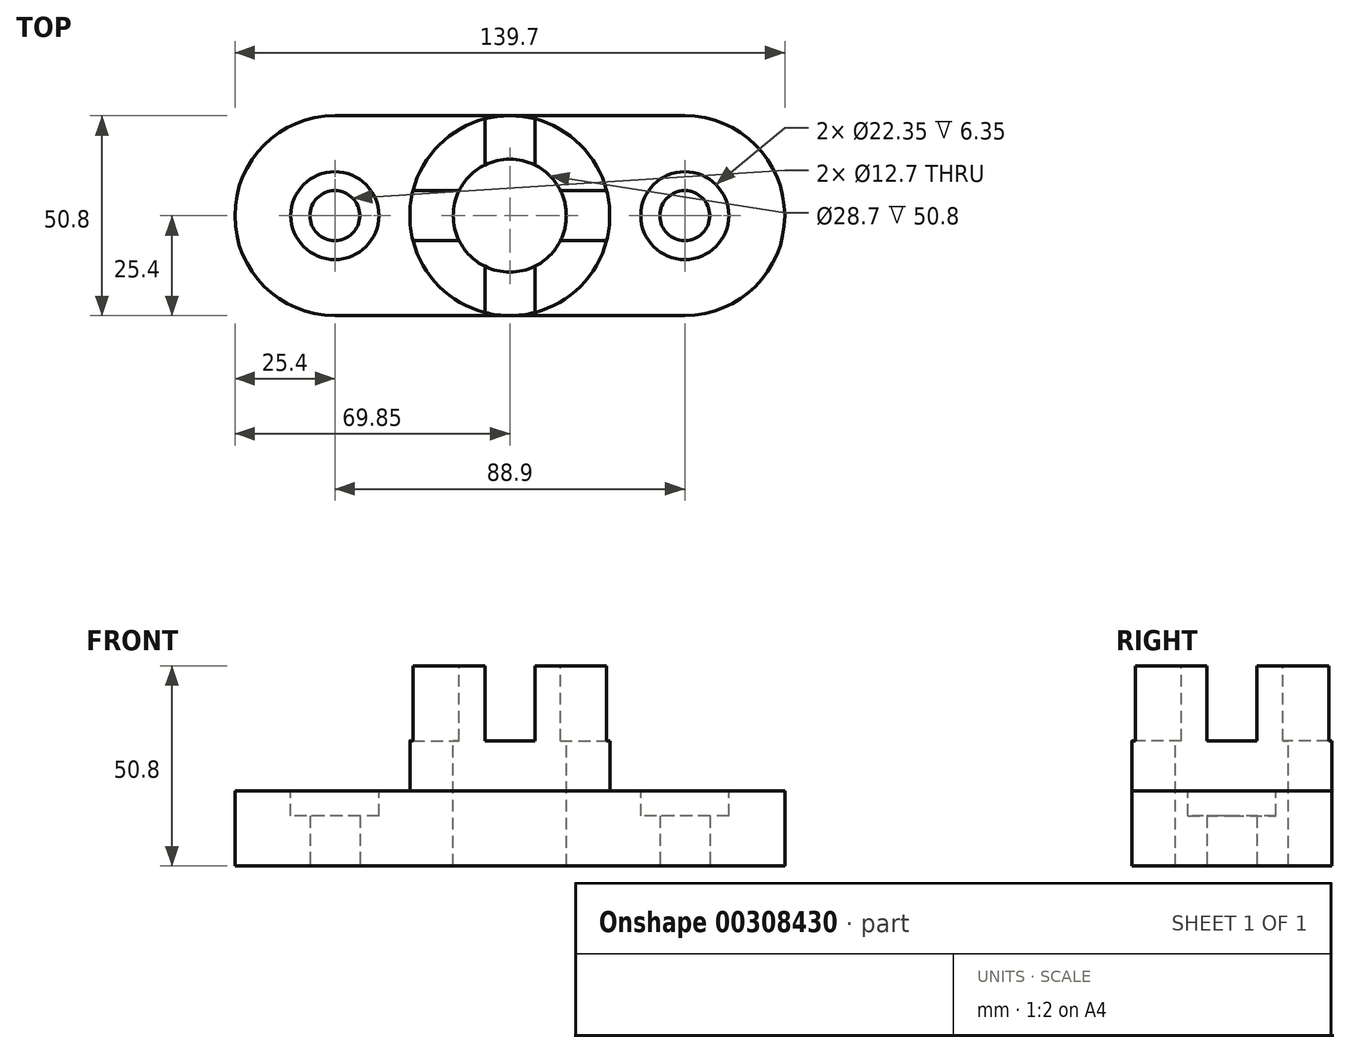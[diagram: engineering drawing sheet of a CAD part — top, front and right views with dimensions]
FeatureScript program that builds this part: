
annotation { "Feature Type Name" : "Feature", "Feature Type Description" : "" }
export const myFeature = defineFeature(function(context is Context, id is Id, definition is map)
    precondition{}
    {
        {
            var Q0;
            Q0=qCreatedBy(makeId("Front.planeOp"),FACE);
            var sketch = newSketch(context, id + "F0", { "sketchPlane" : qUnion([Q0])});
            skLineSegment(sketch, "E0", {"start": v(0, 0) * mm, "end": v(139.7, 0) * mm});
            skLineSegment(sketch, "E1", {"start": v(139.7, 0) * mm, "end": v(139.7, 19.05) * mm});
            skLineSegment(sketch, "E2", {"start": v(139.7, 19.05) * mm, "end": v(0, 19.05) * mm});
            skLineSegment(sketch, "E3", {"start": v(0, 19.05) * mm, "end": v(0, 0) * mm});
            skLineSegment(sketch, "E4", {"start": v(69.85, 19.05) * mm, "end": v(69.85, 50.8) * mm});
            skPoint(sketch, "E4.endSnap0", {"position": v(69.85, 19.05) * mm});
            skLineSegment(sketch, "E5", {"start": v(69.85, 50.8) * mm, "end": v(44.45, 50.8) * mm});
            skLineSegment(sketch, "E6", {"start": v(44.45, 50.8) * mm, "end": v(44.45, 19.05) * mm});
            skLineSegment(sketch, "E7", {"start": v(44.45, 19.05) * mm, "end": v(95.25, 19.05) * mm});
            skLineSegment(sketch, "E8", {"start": v(95.25, 19.05) * mm, "end": v(95.25, 50.8) * mm});
            skLineSegment(sketch, "E9", {"start": v(69.85, 50.8) * mm, "end": v(95.25, 50.8) * mm});
            skSolve(sketch);
        }
        {
            var Q0;
            Q0 = qSketchRegion(id + "F0", true);
            extrude(context, id + "F1", {"entities" : qUnion([Q0]), "depth" : 50.8 * mm});
        }
        {
            var Q0;
            Q0=makeQuery(id+"F1.opExtrude","SWEPT_FACE",FACE,{"disambiguationData":[OSD([sQuery(id+"F0.wireOp",EDGE,"E5"),sQuery(id+"F0.wireOp",EDGE,"E9")])]});
            var sketch = newSketch(context, id + "F2", { "sketchPlane" : qUnion([Q0])});
            skLineSegment(sketch, "E10", {"start": v(95.25, -25.4) * mm, "end": v(69.85, -25.4) * mm});
            skPoint(sketch, "E10.endSnap0", {"position": v(95.25, -25.4) * mm});
            skCircle(sketch, "E11", {"center": v(69.85, -25.4) * mm, "radius": 14.35 * mm});
            skSolve(sketch);
        }
        {
            var Q0;
            Q0 = qSketchRegion(id + "F2", true);
            extrude(context, id + "F3", {"entities" : qUnion([Q0]), "operationType" : NewBodyOperationType.REMOVE, "oppositeDirection" : true, "depth" : 101.6 * mm});
        }
        {
            var Q0;
            Q0=makeQuery(id+"F1.opExtrude","CAP_FACE",FACE,{"disambiguationData":[OSD([sQuery(id+"F0.wireOp",EDGE,"E0"),sQuery(id+"F0.wireOp",EDGE,"E1"),sQuery(id+"F0.wireOp",EDGE,"E2"),sQuery(id+"F0.wireOp",EDGE,"E3"),sQuery(id+"F0.wireOp",EDGE,"E5"),sQuery(id+"F0.wireOp",EDGE,"E6"),sQuery(id+"F0.wireOp",EDGE,"E8"),sQuery(id+"F0.wireOp",EDGE,"E9")])],"isStart":false});
            var sketch = newSketch(context, id + "F4", { "sketchPlane" : qUnion([Q0])});
            skLineSegment(sketch, "E12", {"start": v(44.45, 50.8) * mm, "end": v(44.45, 31.75) * mm});
            skLineSegment(sketch, "E13", {"start": v(44.45, 31.75) * mm, "end": v(63.5, 31.75) * mm});
            skLineSegment(sketch, "E14", {"start": v(63.5, 31.75) * mm, "end": v(63.5, 50.8) * mm});
            skLineSegment(sketch, "E15", {"start": v(63.5, 50.8) * mm, "end": v(76.2, 50.8) * mm});
            skLineSegment(sketch, "E16", {"start": v(76.2, 50.8) * mm, "end": v(76.2, 31.75) * mm});
            skLineSegment(sketch, "E17", {"start": v(76.2, 31.75) * mm, "end": v(63.5, 31.75) * mm});
            skSolve(sketch);
        }
        {
            var Q0;
            Q0 = qSketchRegion(id + "F4", true);
            extrude(context, id + "F5", {"entities" : qUnion([Q0]), "operationType" : NewBodyOperationType.REMOVE, "oppositeDirection" : true, "depth" : 254 * mm});
        }
        {
            var Q0;
            Q0=makeQuery(id+"F1.opExtrude","SWEPT_FACE",FACE,{"disambiguationData":[OSD([sQuery(id+"F0.wireOp",EDGE,"E8")])]});
            var sketch = newSketch(context, id + "F6", { "sketchPlane" : qUnion([Q0])});
            skLineSegment(sketch, "E18", {"start": v(-50.8, 50.8) * mm, "end": v(-31.75, 50.8) * mm});
            skLineSegment(sketch, "E19", {"start": v(-31.75, 50.8) * mm, "end": v(-19.05, 50.8) * mm});
            skLineSegment(sketch, "E20", {"start": v(-19.05, 50.8) * mm, "end": v(-19.05, 31.75) * mm});
            skLineSegment(sketch, "E21", {"start": v(-19.05, 31.75) * mm, "end": v(-31.75, 31.75) * mm});
            skLineSegment(sketch, "E22", {"start": v(-31.75, 31.75) * mm, "end": v(-31.75, 50.8) * mm});
            skSolve(sketch);
        }
        {
            var Q0;
            Q0 = qSketchRegion(id + "F6", true);
            extrude(context, id + "F7", {"entities" : qUnion([Q0]), "operationType" : NewBodyOperationType.REMOVE, "oppositeDirection" : true, "depth" : 127 * mm});
        }
        {
            var Q0;
            {var subQ0=sQuery(id+"F0.wireOp",EDGE,"E2");Q0=makeQuery(id+"F1.opExtrude","SWEPT_FACE",FACE,{"disambiguationData":[OSD([subQ0]),TDD([makeQuery(id+"F0.imprint","IMPRINT",EDGE,{"disambiguationData":[TD([[makeQuery(id+"F0.imprint","INTERSECT",VERTEX,{"derivedFrom":[sQuery(id+"F0.wireOp",EDGE,"E1"),subQ0]}),-1.0]])],"derivedFrom":subQ0})])]});}
            var sketch = newSketch(context, id + "F8", { "sketchPlane" : qUnion([Q0])});
            skLineSegment(sketch, "E23", {"start": v(139.7, -50.8) * mm, "end": v(114.3, -50.8) * mm});
            skLineSegment(sketch, "E24", {"start": v(114.3, -50.8) * mm, "end": v(114.3, -25.4) * mm});
            skCircle(sketch, "E25", {"center": v(114.3, -25.4) * mm, "radius": 11.18 * mm});
            skSolve(sketch);
        }
        {
            var Q0;
            Q0 = qSketchRegion(id + "F8", true);
            extrude(context, id + "F9", {"entities" : qUnion([Q0]), "operationType" : NewBodyOperationType.REMOVE, "oppositeDirection" : true, "depth" : 6.35 * mm});
        }
        {
            var Q0;
            {var subQ0=sQuery(id+"F0.wireOp",EDGE,"E2");Q0=makeQuery(id+"F1.opExtrude","SWEPT_FACE",FACE,{"disambiguationData":[OSD([subQ0]),TDD([makeQuery(id+"F0.imprint","IMPRINT",EDGE,{"disambiguationData":[TD([[makeQuery(id+"F0.imprint","INTERSECT",VERTEX,{"derivedFrom":[subQ0,sQuery(id+"F0.wireOp",EDGE,"E3")]}),1.0]])],"derivedFrom":subQ0})])]});}
            var sketch = newSketch(context, id + "F10", { "sketchPlane" : qUnion([Q0])});
            skLineSegment(sketch, "E26", {"start": v(0, -50.8) * mm, "end": v(25.4, -50.8) * mm});
            skLineSegment(sketch, "E27", {"start": v(25.4, -50.8) * mm, "end": v(25.4, -25.4) * mm});
            skCircle(sketch, "E28", {"center": v(25.4, -25.4) * mm, "radius": 11.18 * mm});
            skSolve(sketch);
        }
        {
            var Q0;
            Q0 = qSketchRegion(id + "F10", true);
            extrude(context, id + "F11", {"entities" : qUnion([Q0]), "operationType" : NewBodyOperationType.REMOVE, "oppositeDirection" : true, "depth" : 6.35 * mm});
        }
        {
            var Q0;
            Q0=makeQuery(id+"F1.opExtrude","SWEPT_FACE",FACE,{"disambiguationData":[OSD([sQuery(id+"F0.wireOp",EDGE,"E0")])]});
            var sketch = newSketch(context, id + "F12", { "sketchPlane" : qUnion([Q0])});
            skLineSegment(sketch, "E29", {"start": v(0, 0) * mm, "end": v(25.4, 0) * mm});
            skLineSegment(sketch, "E30", {"start": v(25.4, 0) * mm, "end": v(25.4, 25.4) * mm});
            skCircle(sketch, "E31", {"center": v(25.4, 25.4) * mm, "radius": 6.35 * mm});
            skSolve(sketch);
        }
        {
            var Q0;
            Q0 = qSketchRegion(id + "F12", true);
            extrude(context, id + "F13", {"entities" : qUnion([Q0]), "operationType" : NewBodyOperationType.REMOVE, "oppositeDirection" : true, "depth" : 50.8 * mm});
        }
        {
            var Q0;
            Q0=makeQuery(id+"F1.opExtrude","SWEPT_FACE",FACE,{"disambiguationData":[OSD([sQuery(id+"F0.wireOp",EDGE,"E0")])]});
            var sketch = newSketch(context, id + "F14", { "sketchPlane" : qUnion([Q0])});
            skLineSegment(sketch, "E32", {"start": v(139.7, 0) * mm, "end": v(114.3, 0) * mm});
            skLineSegment(sketch, "E33", {"start": v(114.3, 0) * mm, "end": v(114.3, 25.4) * mm});
            skCircle(sketch, "E34", {"center": v(114.3, 25.4) * mm, "radius": 6.35 * mm});
            skSolve(sketch);
        }
        {
            var Q0;
            Q0 = qSketchRegion(id + "F14", true);
            extrude(context, id + "F15", {"entities" : qUnion([Q0]), "operationType" : NewBodyOperationType.REMOVE, "oppositeDirection" : true, "depth" : 558.8 * mm});
        }
        {
            var Q0;
            Q0=makeQuery(id+"F1.opExtrude","CAP_EDGE",EDGE,{"disambiguationData":[OSD([sQuery(id+"F0.wireOp",EDGE,"E8")])],"isStart":true});
            var Q1;
            Q1=makeQuery(id+"F1.opExtrude","CAP_EDGE",EDGE,{"disambiguationData":[OSD([sQuery(id+"F0.wireOp",EDGE,"E8")])],"isStart":false});
            var Q2;
            Q2=makeQuery(id+"F1.opExtrude","CAP_EDGE",EDGE,{"disambiguationData":[OSD([sQuery(id+"F0.wireOp",EDGE,"E6")])],"isStart":true});
            var Q3;
            Q3=makeQuery(id+"F1.opExtrude","CAP_EDGE",EDGE,{"disambiguationData":[OSD([sQuery(id+"F0.wireOp",EDGE,"E6")])],"isStart":false});
            var Q4;
            Q4=makeQuery(id+"F1.opExtrude","CAP_EDGE",EDGE,{"disambiguationData":[OSD([sQuery(id+"F0.wireOp",EDGE,"E3")])],"isStart":false});
            var Q5;
            Q5=makeQuery(id+"F1.opExtrude","CAP_EDGE",EDGE,{"disambiguationData":[OSD([sQuery(id+"F0.wireOp",EDGE,"E3")])],"isStart":true});
            var Q6;
            Q6=makeQuery(id+"F1.opExtrude","CAP_EDGE",EDGE,{"disambiguationData":[OSD([sQuery(id+"F0.wireOp",EDGE,"E1")])],"isStart":false});
            var Q7;
            Q7=makeQuery(id+"F1.opExtrude","CAP_EDGE",EDGE,{"disambiguationData":[OSD([sQuery(id+"F0.wireOp",EDGE,"E1")])],"isStart":true});
            fillet(context, id + "F16", {"entities" : qUnion([Q0, Q1, Q2, Q3, Q4, Q5, Q6, Q7]), "radius" : 25.4 * mm, "tangentPropagation" : true, "allowEdgeOverflow" : false});
        }
    });
